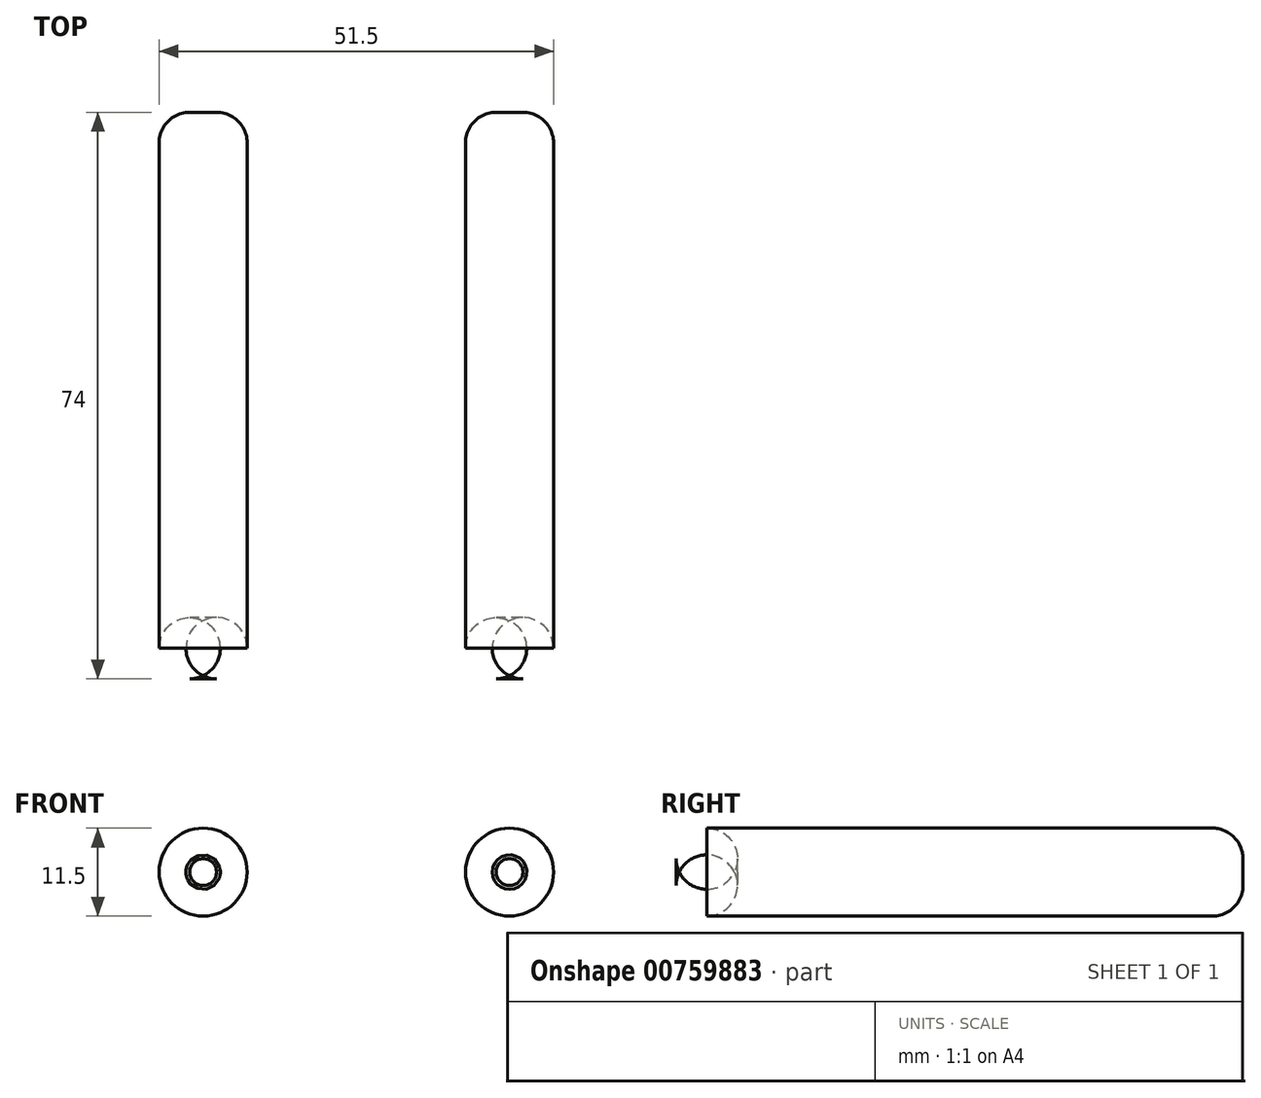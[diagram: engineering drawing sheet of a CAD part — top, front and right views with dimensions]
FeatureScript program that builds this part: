
annotation { "Feature Type Name" : "Feature", "Feature Type Description" : "" }
export const myFeature = defineFeature(function(context is Context, id is Id, definition is map)
    precondition{}
    {
        {
            var Q0;
            Q0=qCreatedBy(makeId("Top.planeOp"),FACE);
            var sketch = newSketch(context, id + "F0", { "sketchPlane" : qUnion([Q0])});
            skCircle(sketch, "E0", {"center": v(-31.25, -8.72) * mm, "radius": 2.87 * mm});
            skSolve(sketch);
        }
        {
            var Q0;
            Q0=makeQuery(id+"F0.imprint","IMPRINT",FACE,{"disambiguationData":[TD([[makeQuery(id+"F0.imprint","IMPRINT",EDGE,{"derivedFrom":sQuery(id+"F0.wireOp",EDGE,"E0")}),1.0]])]});
            extrude(context, id + "F1", {"entities" : qUnion([Q0]), "depth" : 36 * mm, "offsetDistance" : 25 * mm, "hasSecondDirection" : true, "secondDirectionOppositeDirection" : true, "secondDirectionDepth" : 1 * mm});
        }
        {
            var Q0;
            Q0=qCreatedBy(makeId("Right.planeOp"),FACE);
            var sketch = newSketch(context, id + "F2", { "sketchPlane" : qUnion([Q0])});
            skLineSegment(sketch, "E1", {"start": v(-11.6, 0) * mm, "end": v(-11.6, 27) * mm});
            skLineSegment(sketch, "E2", {"start": v(-5.85, 27) * mm, "end": v(-5.85, 0) * mm});
            skLineSegment(sketch, "E3", {"start": v(-8.6, 12) * mm, "end": v(-5.85, 12) * mm});
            skLineSegment(sketch, "E4", {"start": v(-5.72, 16) * mm, "end": v(-8.72, 16) * mm});
            skLineSegment(sketch, "E5", {"start": v(-11.6, 12) * mm, "end": v(-11.6, 13.5) * mm});
            skLineSegment(sketch, "E6", {"start": v(-8.72, 16) * mm, "end": v(-11.72, 16) * mm});
            skLineSegment(sketch, "E7", {"start": v(-11.6, 13.5) * mm, "end": v(-11.6, 15) * mm});
            skLineSegment(sketch, "E8", {"start": v(-11.72, 19) * mm, "end": v(-8.72, 19) * mm});
            skLineSegment(sketch, "E9", {"start": v(-5.85, 15) * mm, "end": v(-5.85, 13.5) * mm});
            skLineSegment(sketch, "E10", {"start": v(-5.72, 19) * mm, "end": v(-8.72, 19) * mm});
            skLineSegment(sketch, "E11", {"start": v(-5.85, 15) * mm, "end": v(-5.85, 12) * mm});
            skLineSegment(sketch, "E12", {"start": v(-11.6, 15) * mm, "end": v(-11.6, 12) * mm});
            skSolve(sketch);
        }
        {
            var Q0;
            {var subQ1=sQuery(id+"F2.wireOp",EDGE,"E4");Q0=makeQuery(id+"F2.imprint","IMPRINT",FACE,{"disambiguationData":[TD([[makeQuery(id+"F2.imprint","IMPRINT",EDGE,{"derivedFrom":subQ1}),-1.0]])]});}
            extrude(context, id + "F3", {"entities" : qUnion([Q0]), "oppositeDirection" : true, "depth" : 31 * mm, "offsetDistance" : 25 * mm});
        }
        {
            var Q0;
            Q0 = qSketchRegion(id + "F2", true);
            extrude(context, id + "F4", {"entities" : qUnion([Q0]), "operationType" : NewBodyOperationType.REMOVE, "oppositeDirection" : true, "depth" : 25 * mm, "offsetDistance" : 25 * mm});
        }
        {
            var Q0;
            Q0=makeQuery(id+"F1.opExtrude","SWEPT_BODY",BODY,{"disambiguationData":[OSD([sQuery(id+"F0.wireOp",EDGE,"E0")])]});
            transform(context, id + "F5", {"entities" : qUnion([Q0]), "transformType" : TransformType.TRANSLATION_3D, "dx" : 25 * mm, "dy" : 0 * mm, "dz" : 0 * mm, "makeCopy" : true});
        }
        {
            var Q0;
            Q0=makeQuery(id+"F3.opExtrude","SWEPT_BODY",BODY,{"disambiguationData":[OSD([sQuery(id+"F2.wireOp",EDGE,"E4"),sQuery(id+"F2.wireOp",EDGE,"E6"),sQuery(id+"F2.wireOp",EDGE,"E8"),sQuery(id+"F2.wireOp",EDGE,"E10"),sQuery(id+"F2.wireOp",EDGE,"E11"),sQuery(id+"F2.wireOp",EDGE,"E12")])]});
            transform(context, id + "F6", {"entities" : qUnion([Q0]), "transformType" : TransformType.TRANSLATION_3D, "dx" : 25 * mm, "dy" : 0 * mm, "dz" : 0 * mm, "makeCopy" : true});
        }
        {
            var Q0;
            Q0=makeQuery(id+"F5.opPattern","COPY",BODY,{"derivedFrom":makeQuery(id+"F1.opExtrude","SWEPT_BODY",BODY,{"disambiguationData":[OSD([sQuery(id+"F0.wireOp",EDGE,"E0")])]}),"instanceName":"1"});
            var Q1;
            Q1=makeQuery(id+"F6.opPattern","COPY",BODY,{"derivedFrom":makeQuery(id+"F3.opExtrude","SWEPT_BODY",BODY,{"disambiguationData":[OSD([sQuery(id+"F2.wireOp",EDGE,"E4"),sQuery(id+"F2.wireOp",EDGE,"E6"),sQuery(id+"F2.wireOp",EDGE,"E8"),sQuery(id+"F2.wireOp",EDGE,"E10"),sQuery(id+"F2.wireOp",EDGE,"E11"),sQuery(id+"F2.wireOp",EDGE,"E12")])]}),"instanceName":"1"});
            deleteBodies(context, id + "F7", {"entities" : qUnion([Q0, Q1])});
        }
        {
            var Q0;
            Q0=makeQuery(id+"F3.opExtrude","SWEPT_BODY",BODY,{"disambiguationData":[OSD([sQuery(id+"F2.wireOp",EDGE,"E4"),sQuery(id+"F2.wireOp",EDGE,"E6"),sQuery(id+"F2.wireOp",EDGE,"E8"),sQuery(id+"F2.wireOp",EDGE,"E10"),sQuery(id+"F2.wireOp",EDGE,"E11"),sQuery(id+"F2.wireOp",EDGE,"E12")])]});
            deleteBodies(context, id + "F8", {"entities" : qUnion([Q0])});
        }
        {
            var Q0;
            Q0=makeQuery(id+"F1.opExtrude","CAP_FACE",FACE,{"disambiguationData":[OSD([sQuery(id+"F0.wireOp",EDGE,"E0")])],"isStart":false});
            var Q1;
            Q1=makeQuery(id+"F1.opExtrude","CAP_FACE",FACE,{"disambiguationData":[OSD([sQuery(id+"F0.wireOp",EDGE,"E0")])],"isStart":true});
            fillet(context, id + "F9", {"entities" : qUnion([Q0, Q1]), "radius" : 2 * mm, "tangentPropagation" : true, "allowEdgeOverflow" : false});
        }
        {
            var Q0;
            Q0=makeQuery(id+"F1.opExtrude","SWEPT_BODY",BODY,{"disambiguationData":[OSD([sQuery(id+"F0.wireOp",EDGE,"E0")])]});
            transform(context, id + "F10", {"entities" : qUnion([Q0]), "transformType" : TransformType.TRANSLATION_3D, "dx" : 20 * mm, "dy" : 0 * mm, "dz" : 0 * mm, "makeCopy" : true});
        }
        {
            var Q0;
            Q0=makeQuery(id+"F1.opExtrude","SWEPT_BODY",BODY,{"disambiguationData":[OSD([sQuery(id+"F0.wireOp",EDGE,"E0")])]});
            var Q1;
            Q1=makeQuery(id+"F10.opPattern","COPY",BODY,{"derivedFrom":makeQuery(id+"F1.opExtrude","SWEPT_BODY",BODY,{"disambiguationData":[OSD([sQuery(id+"F0.wireOp",EDGE,"E0")])]}),"instanceName":"1"});
            var Q2;
            Q2=qCreatedBy(makeId("Origin.pointOp"),VERTEX);
            transform(context, id + "F11", {"entities" : qUnion([Q0, Q1]), "transformType" : TransformType.SCALE_UNIFORMLY, "scale" : 2, "scalePoint" : qUnion([Q2]), "makeCopy" : false});
        }
        {
            var Q0;
            Q0=qCreatedBy(makeId("Top.planeOp"),FACE);
            var sketch = newSketch(context, id + "F12", { "sketchPlane" : qUnion([Q0])});
            skLineSegment(sketch, "E13", {"start": v(-66.06, 0) * mm, "end": v(-14.25, 0) * mm});
            skSolve(sketch);
        }
        {
            var Q0;
            Q0=makeQuery(id+"F1.opExtrude","SWEPT_BODY",BODY,{"disambiguationData":[OSD([sQuery(id+"F0.wireOp",EDGE,"E0")])]});
            var Q1;
            Q1=makeQuery(id+"F10.opPattern","COPY",BODY,{"derivedFrom":makeQuery(id+"F1.opExtrude","SWEPT_BODY",BODY,{"disambiguationData":[OSD([sQuery(id+"F0.wireOp",EDGE,"E0")])]}),"instanceName":"1"});
            var Q2;
            Q2=sQuery(id+"F12.wireOp",EDGE,"E13");
            transform(context, id + "F13", {"entities" : qUnion([Q0, Q1]), "transformType" : TransformType.ROTATION, "transformAxis" : qUnion([Q2]), "angle" : 90 * degree, "oppositeDirection" : true, "makeCopy" : false});
        }
    });
